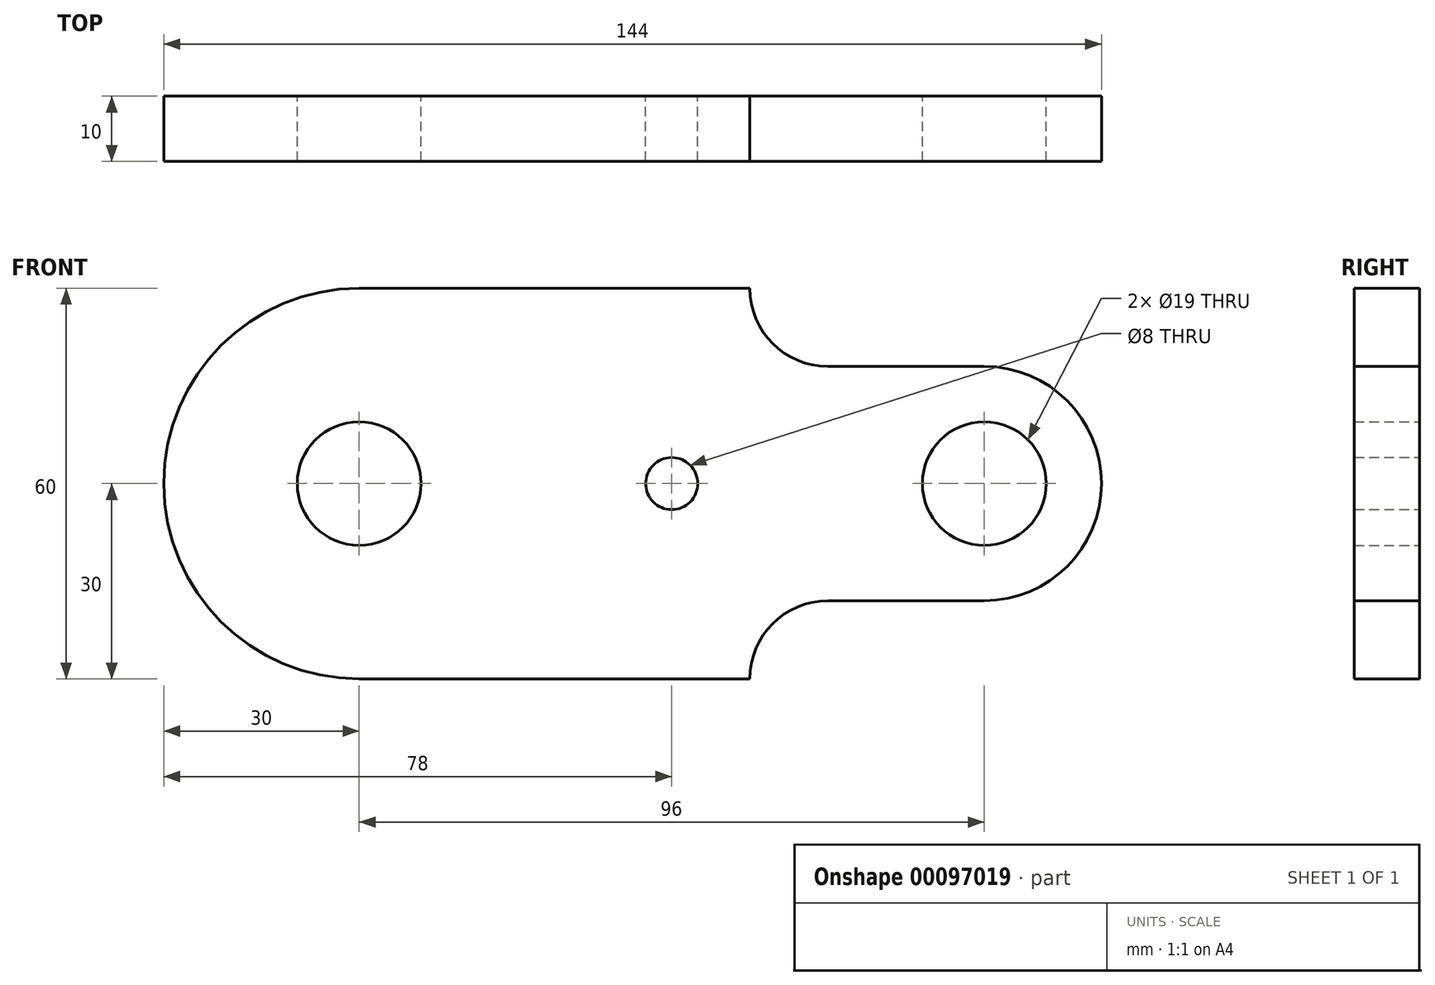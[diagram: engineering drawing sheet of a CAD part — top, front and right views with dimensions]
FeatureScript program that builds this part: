
annotation { "Feature Type Name" : "Feature", "Feature Type Description" : "" }
export const myFeature = defineFeature(function(context is Context, id is Id, definition is map)
    precondition{}
    {
        {
            var Q0;
            Q0=qCreatedBy(makeId("Front.planeOp"),FACE);
            var sketch = newSketch(context, id + "F0", { "sketchPlane" : qUnion([Q0])});
            skCircle(sketch, "E0", {"center": v(0, 0) * mm, "radius": 9.5 * mm});
            skCircle(sketch, "E1", {"center": v(96, 0) * mm, "radius": 9.5 * mm});
            skArc(sketch, "E2", {"start": v(0, 30) * mm, "mid": v(-30, 0) * mm, "end": v(0, -30) * mm});
            skArc(sketch, "E3", {"start": v(96, -18) * mm, "mid": v(114, 0) * mm, "end": v(96, 18) * mm});
            skLineSegment(sketch, "E4", {"start": v(96, -18) * mm, "end": v(72, -18) * mm});
            skLineSegment(sketch, "E5", {"start": v(60, -30) * mm, "end": v(60, -30) * mm});
            skLineSegment(sketch, "E6", {"start": v(60, -30) * mm, "end": v(0, -30) * mm});
            skLineSegment(sketch, "E7", {"start": v(0, 30) * mm, "end": v(60, 30) * mm});
            skLineSegment(sketch, "E8", {"start": v(60, 30) * mm, "end": v(60, 30) * mm});
            skLineSegment(sketch, "E9", {"start": v(72, 18) * mm, "end": v(96, 18) * mm});
            skCircle(sketch, "E10", {"center": v(48, 0) * mm, "radius": 4 * mm});
            skPoint(sketch, "E11.visualSharp", {"position": v(60, 18) * mm});
            skArc(sketch, "E11.filletArc", {"start": v(60, 30) * mm, "mid": v(63.51, 21.51) * mm, "end": v(72, 18) * mm});
            skPoint(sketch, "E12.visualSharp", {"position": v(60, -18) * mm});
            skArc(sketch, "E12.filletArc", {"start": v(72, -18) * mm, "mid": v(63.51, -21.51) * mm, "end": v(60, -30) * mm});
            skSolve(sketch);
        }
        {
            var Q0;
            Q0 = qSketchRegion(id + "F0", true);
            extrude(context, id + "F1", {"entities" : qUnion([Q0]), "depth" : 10 * mm});
        }
    });
